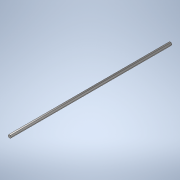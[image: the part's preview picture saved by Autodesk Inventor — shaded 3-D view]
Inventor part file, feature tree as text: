
AUTODESK INVENTOR PART (.ipt)
format: ipt  version: 2020 (Build 240168000, 168)  size: 108,544 bytes
history: native  units: in
note: dims shown in document units (in); Inventor stores cm internally (conversion verified against a paired STEP export)
features: extrude x1, sketch x1
ambient origin geometry x8: Origin, YZ Plane, XZ Plane, XY Plane, X Axis, Y Axis, Z Axis, Center Point
bodies: Solid1 (feature_tree)
feature tree (2):
  extrude  "Extrusion1"  Depth=30.0in TaperAngle=0.0deg
  sketch  "Sketch1"  dims[d0=0.5in d1=30.0in d2=0.0in]
